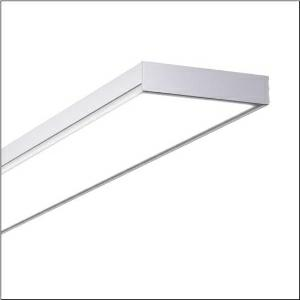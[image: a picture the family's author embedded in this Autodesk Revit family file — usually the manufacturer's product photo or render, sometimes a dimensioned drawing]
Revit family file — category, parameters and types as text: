
# Revit family: apollon_r__31_51mp26wm2441e_c7eb
name_source: partatom
category: Lighting Fixtures
units: mm (PartAtom-declared; Revit-internal decimal feet)

## family parameters
Cut with Voids When Loaded = No
Host = Face
Light Source = No
Part Type = Normal
Room Calculation Point = No
Round Connector Dimension = Use Diameter
Shared = No

## types (1)
- Apollon® 31 (1 x LED, 4600 lm, 33 W, 4000K)
    Apparent Load = 33 VA
    CIE Flux Codes = 61 87 97 97 100
    Color Rendering = 80
    Color Temperature = 4000K
    Default Elevation = 1800 mm
    Description = Apollon® 31, office luminaire, primary optical cover: micro prismatic cover, of PMMA, light emission: direct distribution, primary light characteristic: symmetric, installation type: surface-mounted, LED, rated luminous flux: 4.600lm, luminous efficacy: 139lm/W, light colour: 840, colour temperature: 4000K, control gear: ECG Multilumen, with terminal, 3-pole, mains connection: 220..240V, AC, 50/60Hz, rated input power: 33W, housing, of sheet steel, coil coated, metallic grey (RAL 9006), length: 1.545mm, width: 200mm, height: 44mm, protection rating (complete): IP20, insulation class (complete): insulation class II (safety insulation), certification: CE, impact resistance: IK02, permissible operating ambient temperature: -20..+40°C, packaging unit: 1 piece
    Height = 44 mm
    Lamp = 1 x LED
    Lamp Light Flux = 4600 lm
    Lamp Power = 33 W
    Lamp count = 1
    Length = 1545 mm
    Luminous efficacy = 139 lm/W
    Manufacturer = Siteco
    ModVariant = No
    Model = 51MP26WM2441E
    Mounting Place = Ceiling
    Mounting Type = Surface mounted
    Number of Poles = 1
    OnlyDefault = Yes
    Power Factor = 1
    Product Name = Apollon® 31
    Product group = office luminaire | ceiling mounted
    ProductGroupID = 302
    Protection Class = Protection class II
    Protection Degree = IP 20
    RLX_Detail_Level = 1
    RlxData = <blob elided: 24085 chars, md5=5d7c4909>
    Socket = socket
    Standby Power = 0 W
    System Light Flux = 4600 lm
    System Power = 33 W
    Type Comments = Product without accessories
    Type Image = l_1007091.jpg
    URL = http://relux.com
    VarID = ---
    Voltage = 0 V
    Weight = 0.00 kg
    Width = 200 mm  [stored 0.656168 ft]

note: [stored X ft] marks values corroborated as IEEE doubles in the binary element streams (Revit-internal decimal feet)

## geometry (parser evidence)
native form markers: Blend x4, Sweep x12
no freeform markers — native parametric forms only
